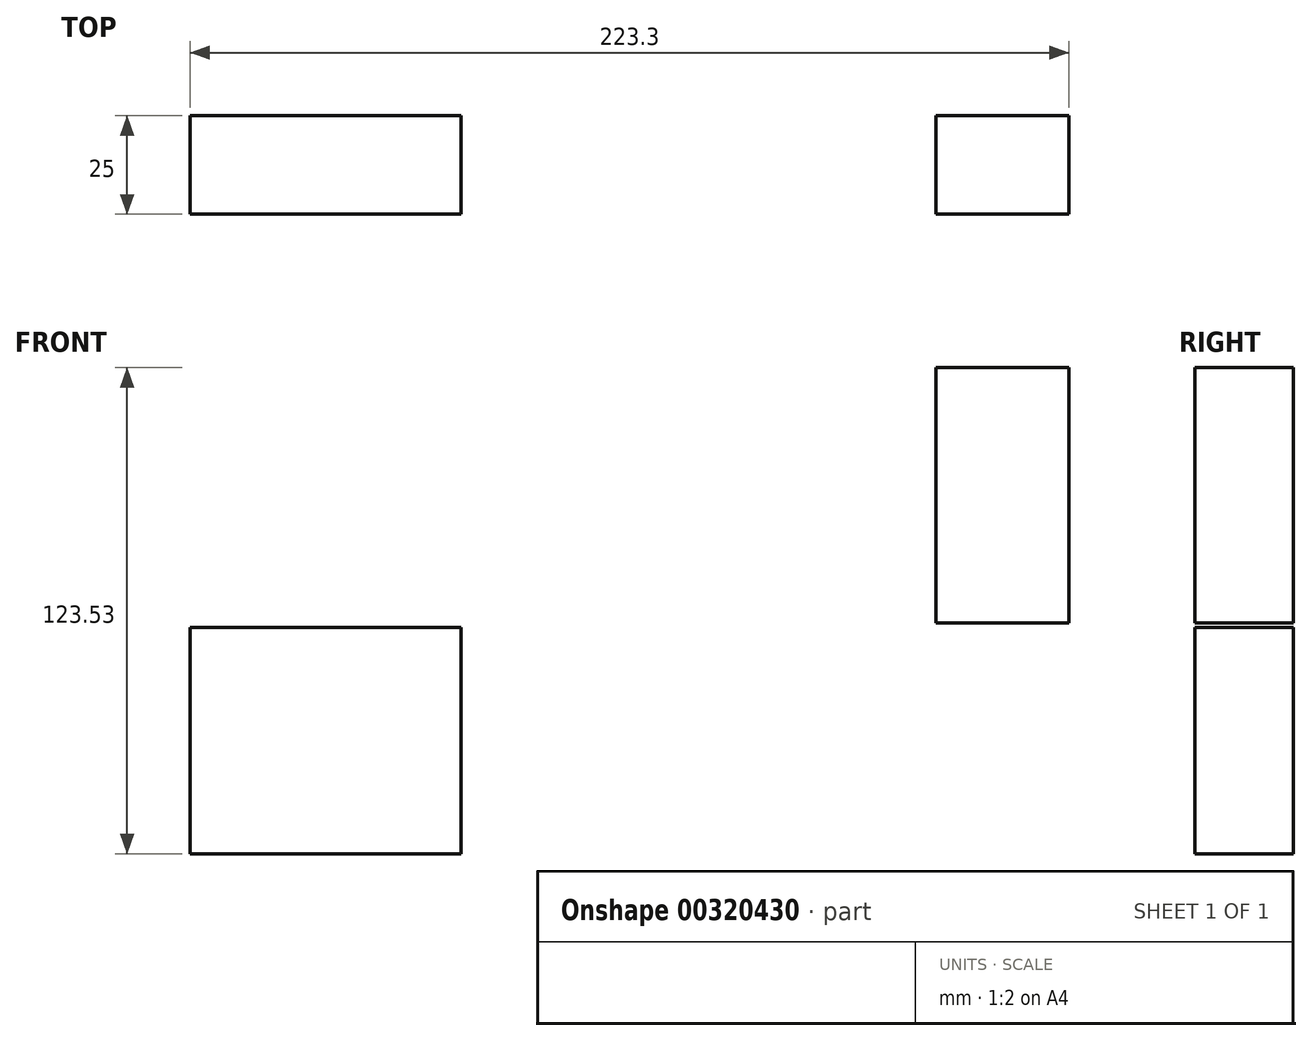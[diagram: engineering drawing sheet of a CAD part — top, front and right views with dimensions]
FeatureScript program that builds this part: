
annotation { "Feature Type Name" : "Feature", "Feature Type Description" : "" }
export const myFeature = defineFeature(function(context is Context, id is Id, definition is map)
    precondition{}
    {
        {
            var Q0;
            Q0=qCreatedBy(makeId("Front.planeOp"),FACE);
            var sketch = newSketch(context, id + "F0", { "sketchPlane" : qUnion([Q0])});
            skLineSegment(sketch, "E0.bottom", {"start": v(-106.46, -4.44) * mm, "end": v(-37.65, -4.44) * mm});
            skLineSegment(sketch, "E0.top", {"start": v(-106.46, 53.07) * mm, "end": v(-37.65, 53.07) * mm});
            skLineSegment(sketch, "E0.left", {"start": v(-106.46, -4.44) * mm, "end": v(-106.46, 53.07) * mm});
            skLineSegment(sketch, "E0.right", {"start": v(-37.65, -4.44) * mm, "end": v(-37.65, 53.07) * mm});
            skPoint(sketch, "E0.middle", {"position": v(-72.05, 24.31) * mm});
            skLineSegment(sketch, "E1.bottom", {"start": v(83.09, 54.17) * mm, "end": v(116.84, 54.17) * mm});
            skLineSegment(sketch, "E1.top", {"start": v(83.09, 119.09) * mm, "end": v(116.84, 119.09) * mm});
            skLineSegment(sketch, "E1.left", {"start": v(83.09, 54.17) * mm, "end": v(83.09, 119.09) * mm});
            skLineSegment(sketch, "E1.right", {"start": v(116.84, 54.17) * mm, "end": v(116.84, 119.09) * mm});
            skPoint(sketch, "E1.middle", {"position": v(99.96, 86.63) * mm});
            skSolve(sketch);
        }
        {
            var Q0;
            Q0=makeQuery(id+"F0.imprint","IMPRINT",FACE,{"disambiguationData":[TD([[makeQuery(id+"F0.imprint","IMPRINT",EDGE,{"derivedFrom":sQuery(id+"F0.wireOp",EDGE,"E0.bottom")}),1.0]])]});
            var Q1;
            Q1=makeQuery(id+"F0.imprint","IMPRINT",FACE,{"disambiguationData":[TD([[makeQuery(id+"F0.imprint","IMPRINT",EDGE,{"derivedFrom":sQuery(id+"F0.wireOp",EDGE,"E1.bottom")}),1.0]])]});
            extrude(context, id + "F1", {"entities" : qUnion([Q0, Q1]), "depth" : 25 * mm});
        }
    });
